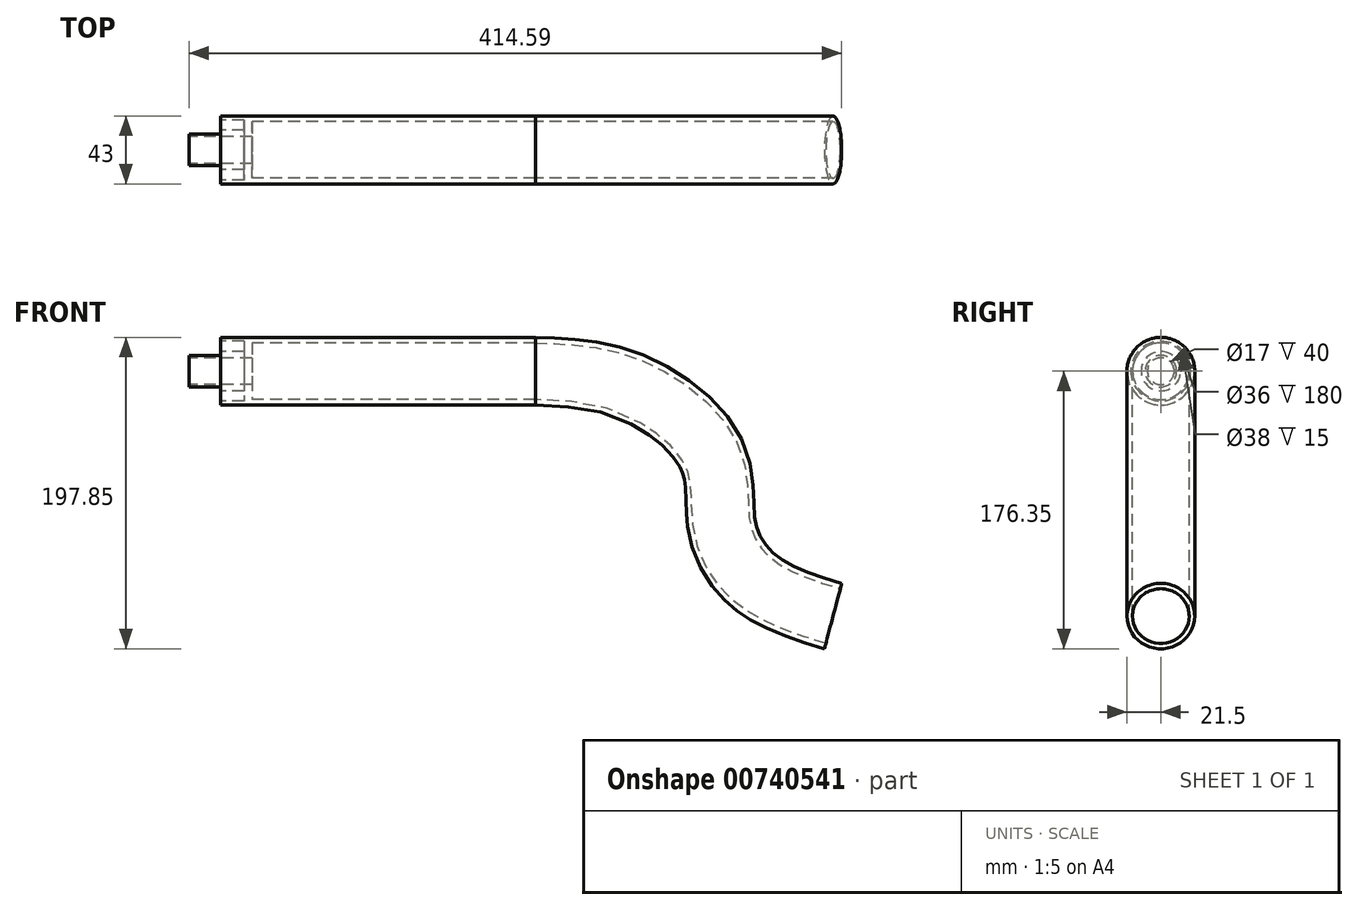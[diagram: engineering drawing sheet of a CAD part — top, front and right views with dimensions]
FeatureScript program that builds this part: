
annotation { "Feature Type Name" : "Feature", "Feature Type Description" : "" }
export const myFeature = defineFeature(function(context is Context, id is Id, definition is map)
    precondition{}
    {
        {
            var Q0;
            Q0=qCreatedBy(makeId("Front.planeOp"),FACE);
            var sketch = newSketch(context, id + "F0", { "sketchPlane" : qUnion([Q0])});
            skLineSegment(sketch, "E0.bottom", {"start": v(0, 0) * mm, "end": v(200, 0) * mm});
            skLineSegment(sketch, "E0.top", {"start": v(0, 21.5) * mm, "end": v(200, 21.5) * mm});
            skLineSegment(sketch, "E0.left", {"start": v(0, 10) * mm, "end": v(0, 21.5) * mm});
            skLineSegment(sketch, "E0.right", {"start": v(200, 18) * mm, "end": v(200, 21.5) * mm});
            skLineSegment(sketch, "E1.bottom", {"start": v(0, 0) * mm, "end": v(-20, 0) * mm});
            skLineSegment(sketch, "E1.top", {"start": v(0, 10) * mm, "end": v(-20, 10) * mm});
            skLineSegment(sketch, "E1.right", {"start": v(-20, 8.5) * mm, "end": v(-20, 10) * mm});
            skLineSegment(sketch, "E2", {"start": v(200, 18) * mm, "end": v(20, 18) * mm});
            skLineSegment(sketch, "E3", {"start": v(20, 18) * mm, "end": v(20, 8.5) * mm});
            skLineSegment(sketch, "E4", {"start": v(20, 8.5) * mm, "end": v(-20, 8.5) * mm});
            skSolve(sketch);
        }
        {
            var Q0;
            Q0=makeQuery(id+"F0.imprint","IMPRINT",FACE,{"disambiguationData":[TD([[makeQuery(id+"F0.imprint","IMPRINT",EDGE,{"derivedFrom":sQuery(id+"F0.wireOp",EDGE,"E0.top")}),-1.0]])]});
            var Q1;
            Q1=sQuery(id+"F0.wireOp",EDGE,"E0.bottom");
            revolve(context, id + "F1", {"surfaceOperationType" : NewSurfaceOperationType.NEW, "entities" : qUnion([Q0]), "axis" : qUnion([Q1]), "revolveType" : RevolveType.FULL});
        }
        {
            var Q0;
            Q0=makeQuery(id+"F1.opRevolve","SWEPT_FACE",FACE,{"disambiguationData":[OSD([sQuery(id+"F0.wireOp",EDGE,"E0.left")])]});
            var sketch = newSketch(context, id + "F2", { "sketchPlane" : qUnion([Q0])});
            skCircle(sketch, "E5", {"center": v(0, 0) * mm, "radius": 19 * mm});
            skCircle(sketch, "E6", {"center": v(0, 0) * mm, "radius": 12.5 * mm});
            skSolve(sketch);
        }
        {
            var Q0;
            Q0=makeQuery(id+"F2.imprint","IMPRINT",FACE,{"disambiguationData":[TD([[makeQuery(id+"F2.imprint","IMPRINT",EDGE,{"derivedFrom":sQuery(id+"F2.wireOp",EDGE,"E5")}),1.0]])]});
            extrude(context, id + "F3", {"entities" : qUnion([Q0]), "operationType" : NewBodyOperationType.REMOVE, "oppositeDirection" : true, "depth" : 15 * mm, "offsetDistance" : 25 * mm});
        }
        {
            var Q0;
            Q0=qCreatedBy(makeId("Front.planeOp"),FACE);
            var sketch = newSketch(context, id + "F4", { "sketchPlane" : qUnion([Q0])});
            skFitSpline(sketch, "E7", {"points": [v(200, 0) * mm, v(259.85, -9.47) * mm, v(312.54, -54.34) * mm, v(318.71, -100.06) * mm, v(341.2, -135.1) * mm, v(389.1, -155.56) * mm], "startDerivative": vector(269.7, -10.13) * mm, "endDerivative": vector(263.84, -80.36) * mm});
            skSolve(sketch);
        }
        {
            var Q0;
            Q0=makeQuery(id+"F1.opRevolve","SWEPT_FACE",FACE,{"disambiguationData":[OSD([sQuery(id+"F0.wireOp",EDGE,"E0.right")])]});
            var sketch = newSketch(context, id + "F5", { "sketchPlane" : qUnion([Q0])});
            skCircle(sketch, "E8", {"center": v(0, 0) * mm, "radius": 18 * mm});
            skCircle(sketch, "E9", {"center": v(0, 0) * mm, "radius": 21.5 * mm});
            skSolve(sketch);
        }
        {
            var Q0;
            Q0=makeQuery(id+"F5.imprint","IMPRINT",FACE,{"disambiguationData":[TD([[makeQuery(id+"F5.imprint","IMPRINT",EDGE,{"derivedFrom":sQuery(id+"F5.wireOp",EDGE,"E8")}),1.0]])]});
            var Q1;
            Q1=sQuery(id+"F4.wireOp",EDGE,"E7");
            sweep(context, id + "F6", {"operationType" : NewBodyOperationType.ADD, "profiles" : qUnion([Q0]), "path" : qUnion([Q1])});
        }
    });
